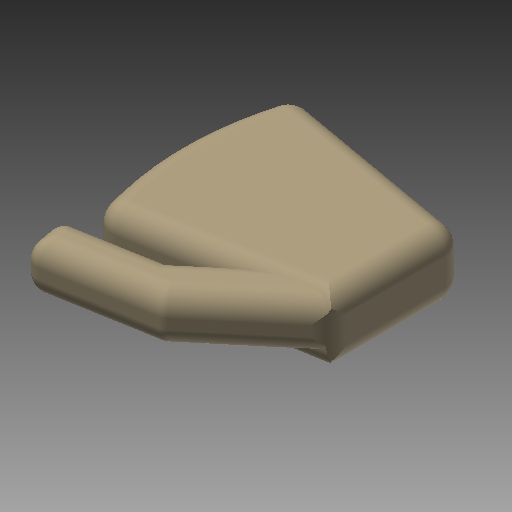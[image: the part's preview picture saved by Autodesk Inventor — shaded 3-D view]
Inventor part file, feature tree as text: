
AUTODESK INVENTOR PART (.ipt)
format: ipt  version: 2022 (Build 260153000, 153)  size: 324,096 bytes
history: native  units: mm (DEFAULTED — no unit token found)
features: fillet x4, other x3, extrude x3, plane x3, sketch x3, mirror x1
ambient origin geometry x8: Origin, YZ Plane, XZ Plane, XY Plane, X Axis, Y Axis, Z Axis, Center Point
bodies: Solid1 (feature_tree)
feature tree (17):
  other  "iMan - 2D BODY"
  extrude  "Extrusion1"  Depth=10.0mm
  extrude  "Extrusion3"  Depth=57.912mm
  mirror  "Mirror1"
  extrude  "Extrusion4"  Depth=28.956mm
  fillet  "Fillet18"  [1 undecoded]
  fillet  "Fillet19"  [1 undecoded]
  fillet  "Fillet20"  Radius=1.4478mm
  fillet  "Fillet21"  [1 undecoded]
  plane  "Work Plane1"
  plane  "Work Plane2"
  other  "Work Axis1"
  plane  "Work Plane3"
  other  "Work Axis2"
  sketch  "Sketch1"  dims[d1=10.0mm d16=96.52mm]
  sketch  "Sketch3"  dims[d17=38.608mm d18=57.912mm]
  sketch  "Sketch4"  dims[d19=3.490659mm d20=28.956mm d21=0.0mm d28=30.0deg d29=1.4478mm d30=0.0mm d35=0.0mm d40=84.455mm d41=-4.3434mm d42=4.3434mm d43=4.3434mm d44=0.0mm d53=8.6868mm d54=5.7912mm d55=8.6868mm d56=14.478mm]
note: 3 required parameter values undecoded (feature->parameter linkage not recoverable at this tier; creation-order binding heuristic only, values carry confidence <= 0.55)
